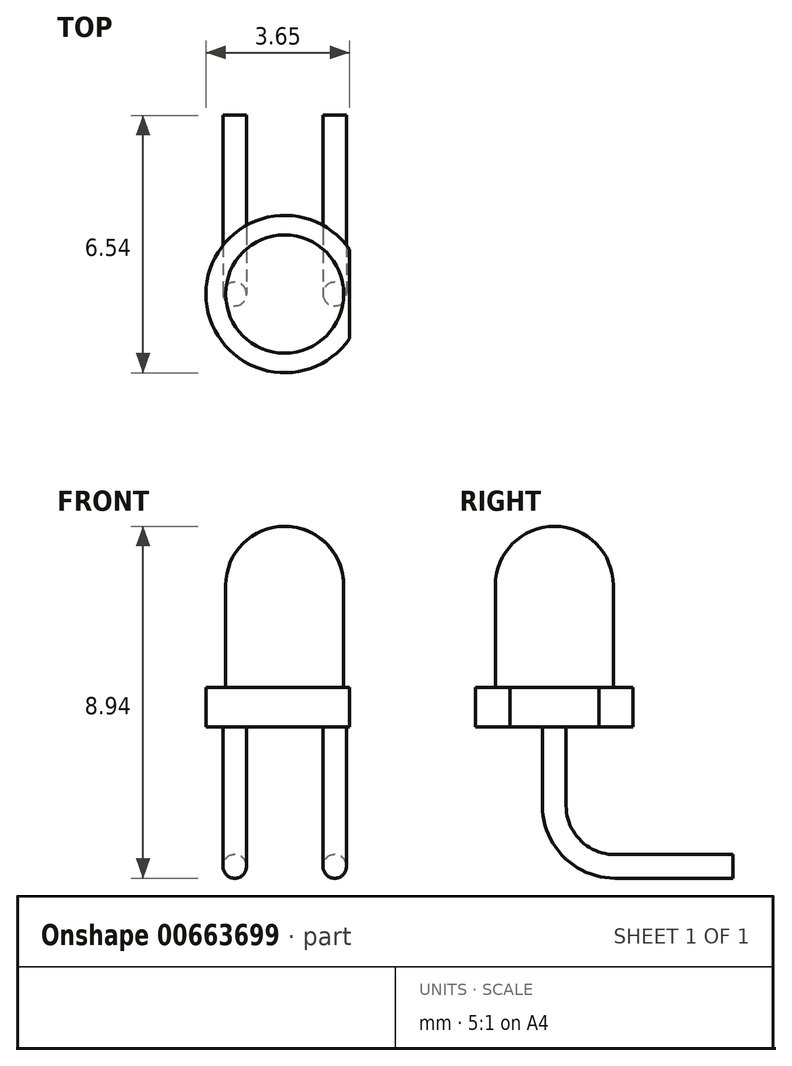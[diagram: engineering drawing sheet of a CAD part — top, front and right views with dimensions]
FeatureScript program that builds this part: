
annotation { "Feature Type Name" : "Feature", "Feature Type Description" : "" }
export const myFeature = defineFeature(function(context is Context, id is Id, definition is map)
    precondition{}
    {
        {
            var Q0;
            Q0=qCreatedBy(makeId("Front.planeOp"),FACE);
            var sketch = newSketch(context, id + "F0", { "sketchPlane" : qUnion([Q0])});
            skLineSegment(sketch, "E0", {"start": v(0, 0) * mm, "end": v(0, 3.6) * mm});
            skLineSegment(sketch, "E1", {"start": v(1.5, 3.6) * mm, "end": v(1.5, 1) * mm});
            skLineSegment(sketch, "E2", {"start": v(1.5, 0) * mm, "end": v(0, 0) * mm});
            skLineSegment(sketch, "E3", {"start": v(1.5, 0) * mm, "end": v(2, 0) * mm});
            skLineSegment(sketch, "E4", {"start": v(2, 0) * mm, "end": v(2, 1) * mm});
            skLineSegment(sketch, "E5", {"start": v(2, 1) * mm, "end": v(1.5, 1) * mm});
            skArc(sketch, "E6", {"start": v(1.5, 3.6) * mm, "mid": v(1.06, 4.66) * mm, "end": v(0, 5.1) * mm});
            skLineSegment(sketch, "E7", {"start": v(0, 5.1) * mm, "end": v(0, 3.6) * mm});
            skSolve(sketch);
        }
        {
            var Q0;
            Q0=qSketchRegion(id+"F0",true);
            var Q1;
            Q1=sQuery(id+"F0.wireOp",EDGE,"E0");
            revolve(context, id + "F1", {"entities" : qUnion([Q0]), "axis" : qUnion([Q1]), "revolveType" : RevolveType.FULL});
        }
        {
            var Q0;
            Q0=qCreatedBy(makeId("Top.planeOp"),FACE);
            var sketch = newSketch(context, id + "F2", { "sketchPlane" : qUnion([Q0])});
            skCircle(sketch, "E8", {"center": v(-1.27, 0) * mm, "radius": 0.3 * mm});
            skCircle(sketch, "E9", {"center": v(1.27, 0) * mm, "radius": 0.3 * mm});
            skLineSegment(sketch, "E10", {"start": v(1.65, 0) * mm, "end": v(1.65, -1.2) * mm});
            skLineSegment(sketch, "E11", {"start": v(1.65, 0) * mm, "end": v(1.65, 1.42) * mm});
            skCircle(sketch, "E12.0", {"center": v(0, 0) * mm, "radius": 2 * mm});
            skSolve(sketch);
        }
        {
            var Q0;
            Q0=makeQuery(id+"F2.imprint","IMPRINT",FACE,{"disambiguationData":[TD([[makeQuery(id+"F2.imprint","IMPRINT",EDGE,{"derivedFrom":sQuery(id+"F2.wireOp",EDGE,"E8")}),1.0]])]});
            var Q1;
            Q1=makeQuery(id+"F2.imprint","IMPRINT",FACE,{"disambiguationData":[TD([[makeQuery(id+"F2.imprint","IMPRINT",EDGE,{"derivedFrom":sQuery(id+"F2.wireOp",EDGE,"E9")}),1.0]])]});
            extrude(context, id + "F3", {"entities" : qUnion([Q0, Q1]), "operationType" : NewBodyOperationType.ADD, "oppositeDirection" : true, "depth" : 2 * mm, "offsetDistance" : 25 * mm});
        }
        {
            var Q0;
            {var subQ0=sQuery(id+"F2.wireOp",EDGE,"E11");var subQ1=sQuery(id+"F2.wireOp",EDGE,"E10");var subQ2=makeQuery(id+"F2.imprint","INTERSECT",VERTEX,{"derivedFrom":[subQ1,subQ0]});Q0=makeQuery(id+"F2.imprint","IMPRINT",FACE,{"disambiguationData":[TD([[makeQuery(id+"F2.imprint","IMPRINT",EDGE,{"disambiguationData":[TD([[subQ2,-1.0]])],"derivedFrom":subQ1}),1.0]])]});}
            extrude(context, id + "F4", {"entities" : qUnion([Q0]), "operationType" : NewBodyOperationType.REMOVE, "depth" : 25 * mm, "offsetDistance" : 25 * mm});
        }
        {
            var Q0;
            Q0=makeQuery(id+"F3.opExtrude","CAP_FACE",FACE,{"disambiguationData":[OSD([sQuery(id+"F2.wireOp",EDGE,"E8")])],"isStart":false});
            var sketch = newSketch(context, id + "F5", { "sketchPlane" : qUnion([Q0])});
            skCircle(sketch, "E13.0", {"center": v(-1.27, 0) * mm, "radius": 0.3 * mm});
            skCircle(sketch, "E13.1", {"center": v(1.27, 0) * mm, "radius": 0.3 * mm});
            skLineSegment(sketch, "E14", {"start": v(-1.8, -1.54) * mm, "end": v(1.92, -1.54) * mm, "construction": true});
            skSolve(sketch);
        }
        {
            var Q0;
            Q0=makeQuery(id+"F5.imprint","IMPRINT",FACE,{"disambiguationData":[TD([[makeQuery(id+"F5.imprint","IMPRINT",EDGE,{"derivedFrom":sQuery(id+"F5.wireOp",EDGE,"E13.0")}),-1.0]])]});
            var Q1;
            Q1=makeQuery(id+"F5.imprint","IMPRINT",FACE,{"disambiguationData":[TD([[makeQuery(id+"F5.imprint","IMPRINT",EDGE,{"derivedFrom":sQuery(id+"F5.wireOp",EDGE,"E13.1")}),1.0]])]});
            var Q2;
            Q2=qSketchRegion(id+"F7",true);
            var Q3;
            Q3=sQuery(id+"F5.wireOp",EDGE,"E14");
            var Q4;
            Q4=sQuery(id+"F5.wireOp",EDGE,"E14");
            revolve(context, id + "F6", {"operationType" : NewBodyOperationType.ADD, "entities" : qUnion([Q0, Q1, Q2]), "surfaceEntities" : qUnion([Q3]), "axis" : qUnion([Q4]), "revolveType" : RevolveType.ONE_DIRECTION, "angle" : 90 * degree});
        }
        {
            var Q0;
            Q0=makeQuery(id+"F6.opRevolve","CAP_FACE",FACE,{"disambiguationData":[OSD([sQuery(id+"F5.wireOp",EDGE,"E13.1")])],"isStart":false});
            var sketch = newSketch(context, id + "F7", { "sketchPlane" : qUnion([Q0])});
            skCircle(sketch, "E15.0", {"center": v(-1.27, -3.54) * mm, "radius": 0.3 * mm});
            skSolve(sketch);
        }
        {
            var Q0;
            Q0=makeQuery(id+"F6.opRevolve","CAP_FACE",FACE,{"disambiguationData":[OSD([sQuery(id+"F5.wireOp",EDGE,"E13.0")])],"isStart":false});
            var Q1;
            Q1=makeQuery(id+"F7.imprint","IMPRINT",FACE,{"disambiguationData":[TD([[makeQuery(id+"F7.imprint","IMPRINT",EDGE,{"derivedFrom":sQuery(id+"F7.wireOp",EDGE,"E15.0")}),1.0]])]});
            extrude(context, id + "F8", {"entities" : qUnion([Q0, Q1]), "operationType" : NewBodyOperationType.ADD, "depth" : 3 * mm, "offsetDistance" : 25 * mm});
        }
    });
